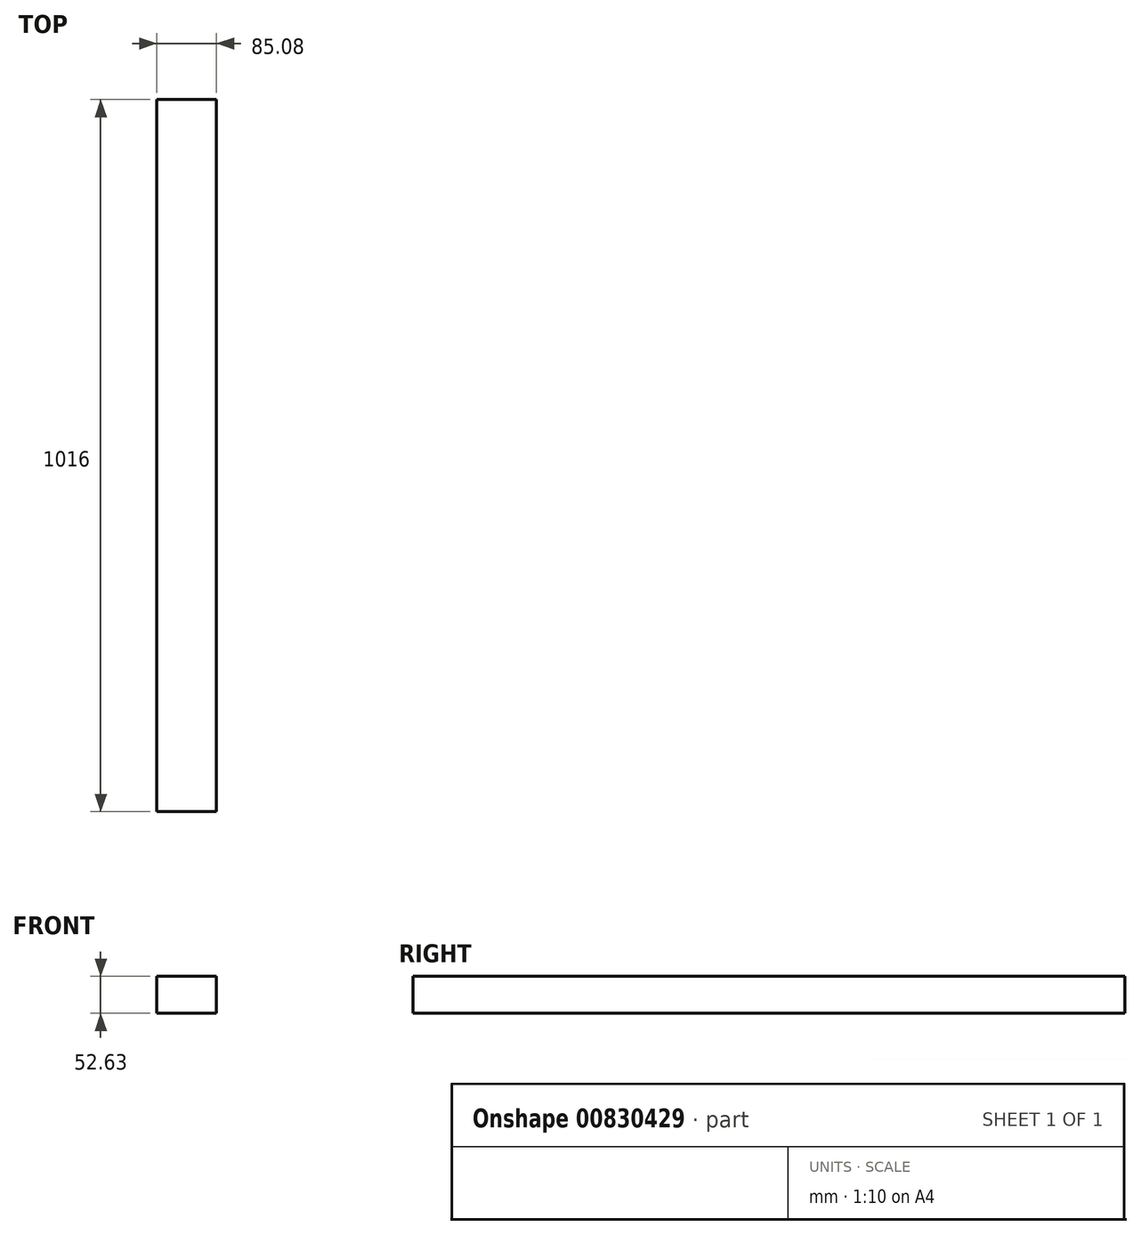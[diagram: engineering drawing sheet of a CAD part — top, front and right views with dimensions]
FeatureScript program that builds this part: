
annotation { "Feature Type Name" : "Feature", "Feature Type Description" : "" }
export const myFeature = defineFeature(function(context is Context, id is Id, definition is map)
    precondition{}
    {
        {
            var Q0;
            Q0=qCreatedBy(makeId("Front.planeOp"),FACE);
            var sketch = newSketch(context, id + "F0", { "sketchPlane" : qUnion([Q0])});
            skLineSegment(sketch, "E0.bottom", {"start": v(0, 0) * mm, "end": v(85.08, 0) * mm});
            skLineSegment(sketch, "E0.top", {"start": v(0, 52.63) * mm, "end": v(85.08, 52.63) * mm});
            skLineSegment(sketch, "E0.left", {"start": v(0, 0) * mm, "end": v(0, 52.63) * mm});
            skLineSegment(sketch, "E0.right", {"start": v(85.08, 0) * mm, "end": v(85.08, 52.63) * mm});
            skSolve(sketch);
        }
        {
            var Q0;
            Q0=makeQuery(id+"F0.imprint","IMPRINT",FACE,{"disambiguationData":[TD([[makeQuery(id+"F0.imprint","IMPRINT",EDGE,{"derivedFrom":sQuery(id+"F0.wireOp",EDGE,"E0.bottom")}),1.0]])]});
            extrude(context, id + "F1", {"entities" : qUnion([Q0]), "depth" : 1016 * mm, "offsetDistance" : 25.4 * mm});
        }
    });
